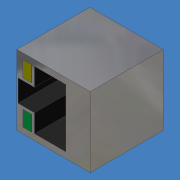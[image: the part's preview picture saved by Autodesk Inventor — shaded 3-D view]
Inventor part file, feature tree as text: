
AUTODESK INVENTOR PART (.ipt)
format: ipt  version: unknown  size: 211,456 bytes
history: native  units: mm (DEFAULTED — no unit token found)
features: extrude x3, sketch x3, mirror x1
ambient origin geometry x8: Origin, YZ Plane, XZ Plane, XY Plane, X Axis, Y Axis, Z Axis, Center Point
feature tree (7):
  extrude  "Extrusion1"  Depth=16.2052mm
  extrude  "Extrusion2"  Depth=13.462mm
  extrude  "Extrusion3"  Depth=3.81mm
  mirror  "Mirror1"
  sketch  "Sketch1"  dims[d0=16.9164mm d1=16.2052mm]
  sketch  "Sketch2"  dims[d2=16.8656mm d3=0.0mm d4=13.462mm]
  sketch  "Sketch3"  dims[d5=0.254mm d6=3.81mm d7=5.08mm d8=5.588mm d9=10.16mm d10=0.0mm d11=0.635mm d12=0.635mm d13=2.032mm d14=0.0254mm d15=0.0mm]
